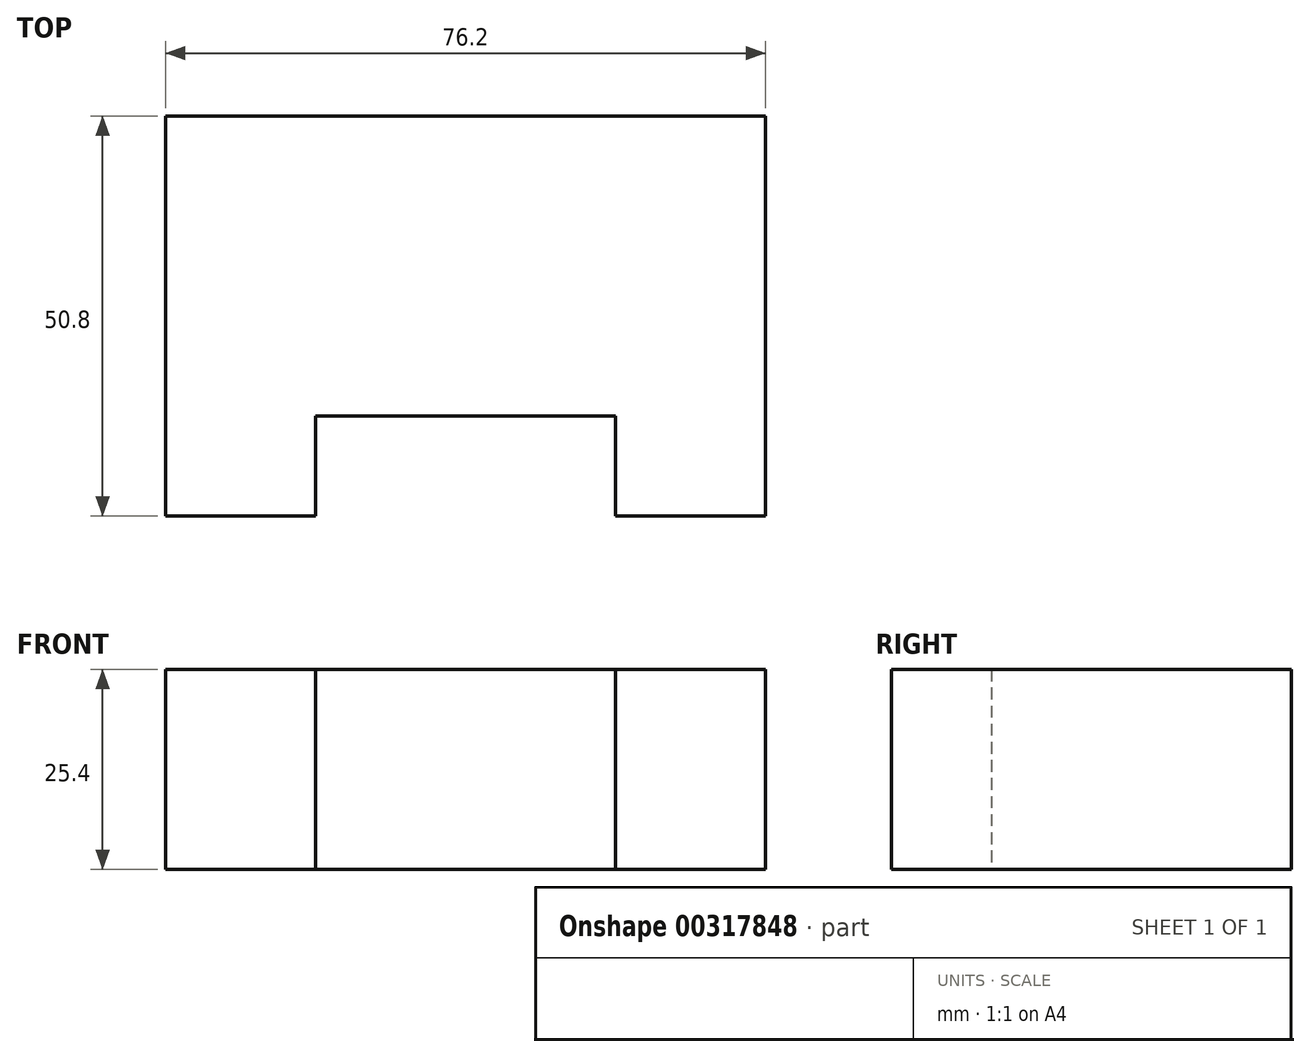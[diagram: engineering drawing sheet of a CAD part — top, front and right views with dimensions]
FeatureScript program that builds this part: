
annotation { "Feature Type Name" : "Feature", "Feature Type Description" : "" }
export const myFeature = defineFeature(function(context is Context, id is Id, definition is map)
    precondition{}
    {
        {
            var Q0;
            Q0=qCreatedBy(makeId("Top.planeOp"),FACE);
            var sketch = newSketch(context, id + "F0", { "sketchPlane" : qUnion([Q0])});
            skLineSegment(sketch, "E0", {"start": v(0, 0) * mm, "end": v(0, 50.8) * mm});
            skLineSegment(sketch, "E1", {"start": v(0, 50.8) * mm, "end": v(76.2, 50.8) * mm});
            skLineSegment(sketch, "E2", {"start": v(76.2, 50.8) * mm, "end": v(76.2, 0) * mm});
            skLineSegment(sketch, "E3", {"start": v(76.2, 0) * mm, "end": v(57.15, 0) * mm});
            skLineSegment(sketch, "E4", {"start": v(57.15, 0) * mm, "end": v(57.15, 12.7) * mm});
            skLineSegment(sketch, "E5", {"start": v(57.15, 12.7) * mm, "end": v(19.05, 12.7) * mm});
            skLineSegment(sketch, "E6", {"start": v(19.05, 12.7) * mm, "end": v(19.05, 0) * mm});
            skLineSegment(sketch, "E7", {"start": v(19.05, 0) * mm, "end": v(0, 0) * mm});
            skLineSegment(sketch, "E8", {"start": v(0, 38.1) * mm, "end": v(76.2, 38.1) * mm});
            skPoint(sketch, "E8.endSnap0", {"position": v(76.2, 25.4) * mm});
            skLineSegment(sketch, "E9", {"start": v(25.4, 50.8) * mm, "end": v(25.4, 38.1) * mm});
            skLineSegment(sketch, "E10", {"start": v(50.8, 50.8) * mm, "end": v(50.8, 38.1) * mm});
            skLineSegment(sketch, "E11", {"start": v(0, 0) * mm, "end": v(38.1, 38.1) * mm});
            skLineSegment(sketch, "E12", {"start": v(38.1, 38.1) * mm, "end": v(76.2, 0) * mm});
            skSolve(sketch);
        }
        {
            var Q0;
            Q0 = qSketchRegion(id + "F0", true);
            extrude(context, id + "F1", {"entities" : qUnion([Q0]), "depth" : 25.4 * mm});
        }
    });
